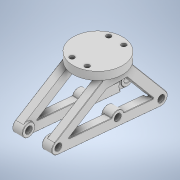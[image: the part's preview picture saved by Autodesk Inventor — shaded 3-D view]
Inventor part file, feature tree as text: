
AUTODESK INVENTOR PART (.ipt)
format: ipt  version: 2021 (Build 250183000, 183)  size: 662,016 bytes
history: native  units: mm
features: extrude x6, sketch x6, fillet x3, plane x1, mirror x1
ambient origin geometry x8: Origin, YZ Plane, XZ Plane, XY Plane, X Axis, Y Axis, Z Axis, Center Point
bodies: Solid1 (feature_tree)
feature tree (17):
  extrude  "Extrusion1"  Depth=8.0mm
  extrude  "Extrusion2"  Depth=5.0mm
  extrude  "Extrusion3"  Depth=55.0mm
  extrude  "Extrusion4"  Depth=16.0mm
  plane  "Work Plane2"
  extrude  "Extrusion5"  Depth=16.0mm
  fillet  "Fillet1"  Radius=22.0mm
  mirror  "Mirror2"
  fillet  "Fillet2"  Radius=36.0mm
  fillet  "Fillet3"  Radius=40.0mm
  extrude  "Extrusion6"  Depth=0.5mm
  sketch  "Sketch1"  dims[d0=8.0mm d1=8.0mm]
  sketch  "Sketch2"  dims[d3=75.0mm d4=5.0mm]
  sketch  "Sketch3"  dims[d7=8.0mm d8=55.0mm]
  sketch  "Sketch4"  dims[d9=7.0mm d12=16.0mm]
  sketch  "Sketch5"  dims[d13=16.0mm d14=16.0mm d15=22.0mm d16=36.0mm d17=40.0mm]
  sketch  "Sketch6"  dims[d20=35.0mm d21=17.5mm d22=50.0mm d23=12.0mm d24=0.920468mm d25=2.085064mm d26=10.0mm d27=0.0mm d28=2.75mm d29=0.0mm d30=26.0mm d31=3.0mm d32=0.0mm d34=16.0mm d35=0.25mm d36=0.0mm d37=12.25mm d38=62.5mm d39=12.25mm d40=10.0mm d41=0.0mm d43=0.5mm d44=0.5mm d45=0.5mm d46=0.5mm d47=6.0mm d48=25.0mm d49=160.0mm d51=360.0deg d53=0.0mm d54=0.0mm]
